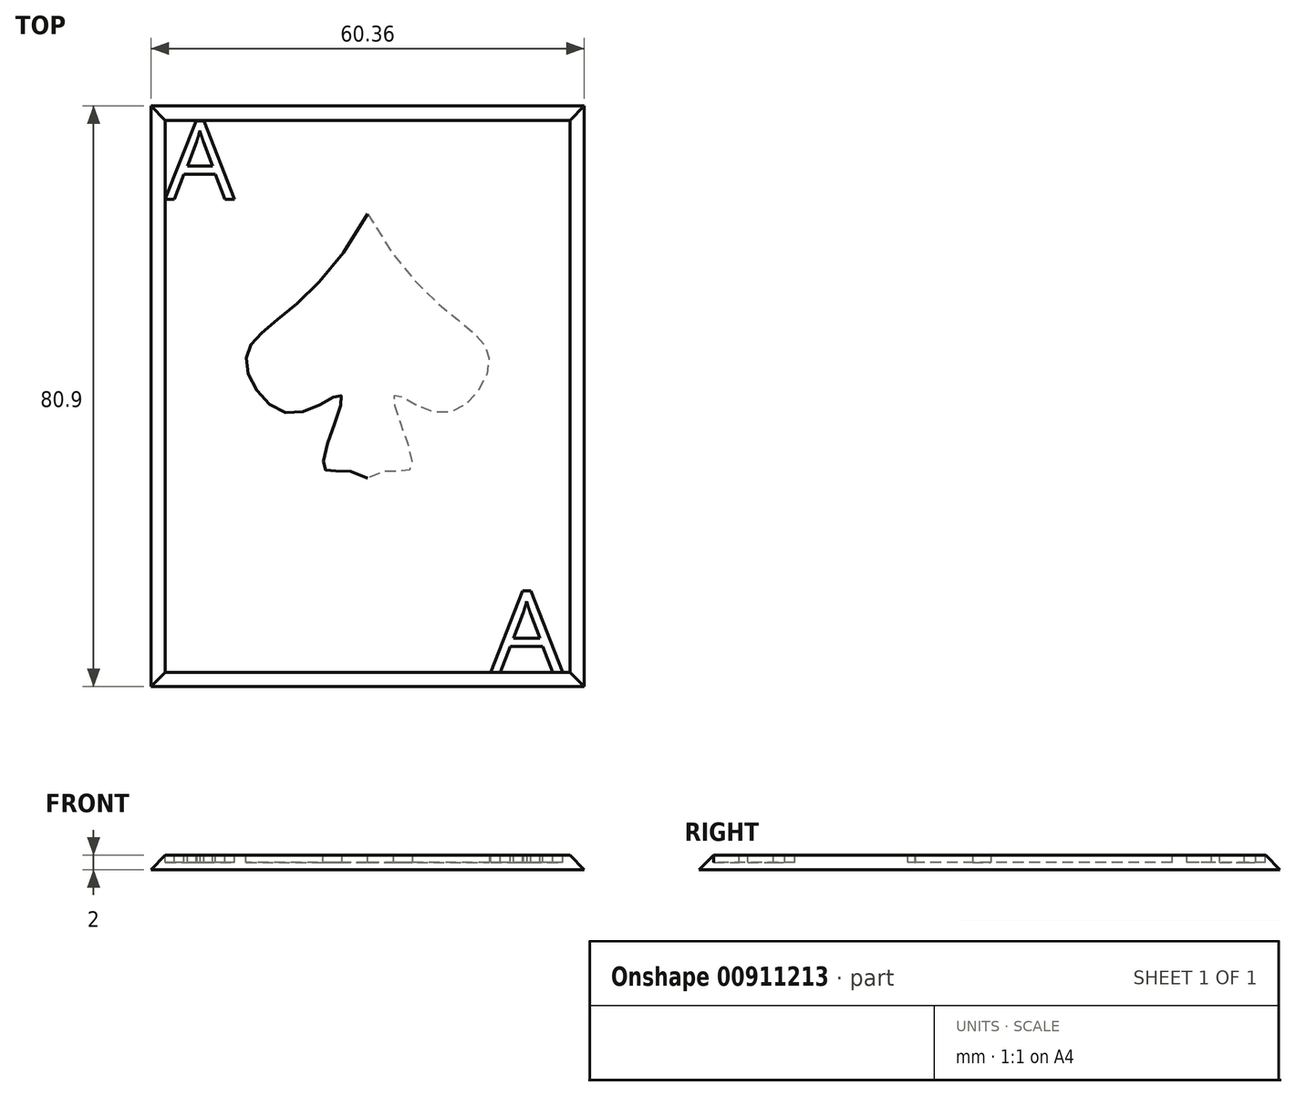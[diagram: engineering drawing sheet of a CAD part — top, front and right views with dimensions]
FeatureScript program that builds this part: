
annotation { "Feature Type Name" : "Feature", "Feature Type Description" : "" }
export const myFeature = defineFeature(function(context is Context, id is Id, definition is map)
    precondition{}
    {
        {
            var Q0;
            Q0=qCreatedBy(makeId("Top.planeOp"),FACE);
            var sketch = newSketch(context, id + "F0", { "sketchPlane" : qUnion([Q0])});
            skLineSegment(sketch, "E0.bottom", {"start": v(-30.17, 40.45) * mm, "end": v(30.18, 40.45) * mm});
            skLineSegment(sketch, "E0.top", {"start": v(-30.18, -40.45) * mm, "end": v(30.17, -40.45) * mm});
            skLineSegment(sketch, "E0.left", {"start": v(-30.17, 40.45) * mm, "end": v(-30.18, -40.45) * mm});
            skLineSegment(sketch, "E0.right", {"start": v(30.18, 40.45) * mm, "end": v(30.17, -40.45) * mm});
            skPoint(sketch, "E0.middle", {"position": v(0, 0) * mm});
            skSolve(sketch);
        }
        {
            var Q0;
            Q0 = qSketchRegion(id + "F0", true);
            extrude(context, id + "F1", {"entities" : qUnion([Q0]), "depth" : 2 * mm, "offsetDistance" : 25 * mm});
        }
        {
            var Q0;
            Q0=makeQuery(id+"F1.opExtrude","CAP_EDGE",EDGE,{"disambiguationData":[OSD([sQuery(id+"F0.wireOp",EDGE,"E0.bottom")])],"isStart":false});
            var Q1;
            Q1=makeQuery(id+"F1.opExtrude","CAP_EDGE",EDGE,{"disambiguationData":[OSD([sQuery(id+"F0.wireOp",EDGE,"E0.right")])],"isStart":false});
            var Q2;
            Q2=makeQuery(id+"F1.opExtrude","CAP_EDGE",EDGE,{"disambiguationData":[OSD([sQuery(id+"F0.wireOp",EDGE,"E0.top")])],"isStart":false});
            var Q3;
            Q3=makeQuery(id+"F1.opExtrude","CAP_EDGE",EDGE,{"disambiguationData":[OSD([sQuery(id+"F0.wireOp",EDGE,"E0.left")])],"isStart":false});
            chamfer(context, id + "F2", {"entities" : qUnion([Q0, Q1, Q2, Q3]), "width" : 2 * mm, "tangentPropagation" : true});
        }
        {
            var Q0;
            Q0=makeQuery(id+"F1.opExtrude","CAP_FACE",FACE,{"disambiguationData":[OSD([sQuery(id+"F0.wireOp",EDGE,"E0.bottom"),sQuery(id+"F0.wireOp",EDGE,"E0.top"),sQuery(id+"F0.wireOp",EDGE,"E0.left"),sQuery(id+"F0.wireOp",EDGE,"E0.right")])],"isStart":false});
            var sketch = newSketch(context, id + "F3", { "sketchPlane" : qUnion([Q0])});
            skFitSpline(sketch, "E1", {"points": [v(0, 25.43) * mm, v(-16.93, 5.14) * mm, v(-10.4, -2.38) * mm, v(-3.64, 0) * mm, v(-6.14, -9.9) * mm, v(0, -11.41) * mm], "startDerivative": vector(-77.57, -142.65) * mm, "endDerivative": vector(53.37, -40.66) * mm});
            skFitSpline(sketch, "E2.MirrorCS", {"points": [v(0, 25.43) * mm, v(16.93, 5.14) * mm, v(10.4, -2.38) * mm, v(3.64, 0) * mm, v(6.14, -9.9) * mm, v(0, -11.41) * mm], "startDerivative": vector(77.57, -142.65) * mm, "endDerivative": vector(-53.37, -40.66) * mm});
            skText(sketch, "E3", { "text": "A", "fontName": "OpenSans-Regular.ttf"});
            skText(sketch, "E4", { "text": "A\n", "fontName": "OpenSans-Regular.ttf"});
            const initialGuessF3  = {"E3": [-0.02818, 0.02747, 1, 0, 0.01097], "E4": [0.01716, -0.03845, 1, 0, 0.01137]};
            skSetInitialGuess(sketch, initialGuessF3);
            skSolve(sketch);
        }
        {
            var Q0;
            Q0 = qSketchRegion(id + "F3", true);
            extrude(context, id + "F4", {"entities" : qUnion([Q0]), "operationType" : NewBodyOperationType.REMOVE, "oppositeDirection" : true, "depth" : 1 * mm, "offsetDistance" : 25 * mm});
        }
    });
